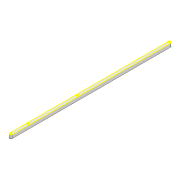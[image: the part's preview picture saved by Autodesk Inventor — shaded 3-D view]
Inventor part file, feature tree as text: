
AUTODESK INVENTOR PART (.ipt)
format: ipt  version: 2022 (Build 260153000, 153)  size: 98,816 bytes
history: native  units: mm
features: sketch x2, extrude x1, projected_geometry x1
ambient origin geometry x8: Origin, YZ Plane, XZ Plane, XY Plane, X Axis, Y Axis, Z Axis, Center Point
bodies: Solid1 (feature_tree)
feature tree (4):
  extrude  "Extrusion1"  Depth=6.0mm
  sketch  "Sketch2"  dims[d2=3.0mm d3=3.0mm d4=8.0mm d5=0.0mm d6=3.0mm d7=145.527mm d8=3.0mm d9=37.934mm]
  sketch  "Sketch1"  dims[d0=347.765mm d1=6.0mm]
  projected_geometry  "Projected Loop1"
